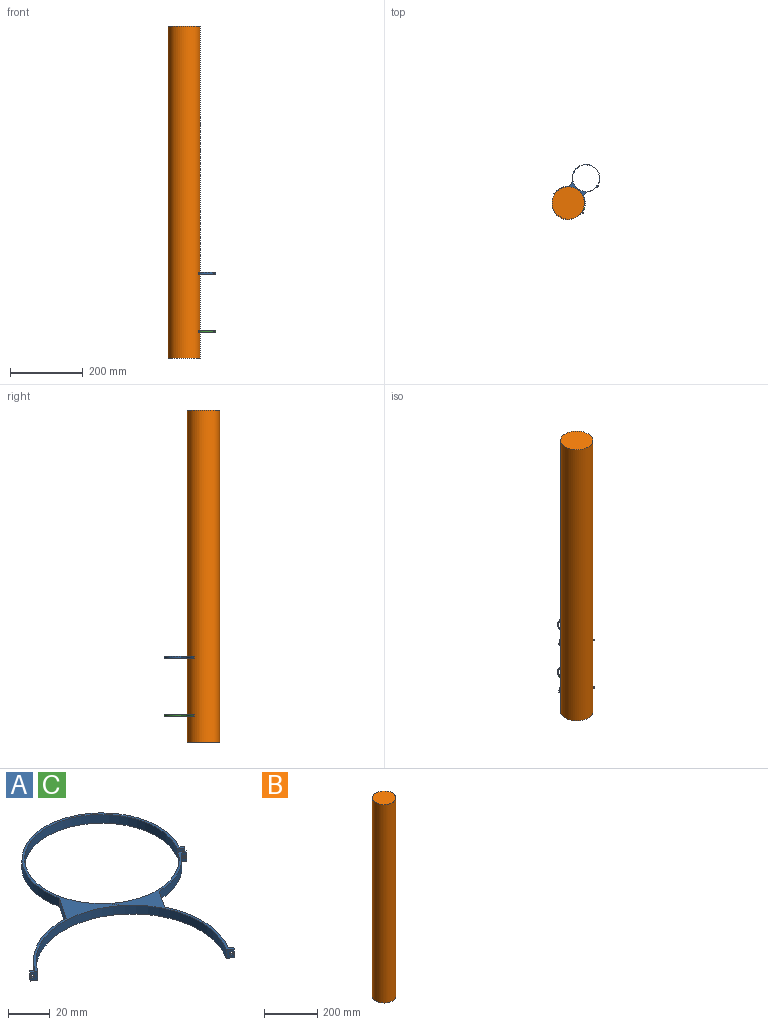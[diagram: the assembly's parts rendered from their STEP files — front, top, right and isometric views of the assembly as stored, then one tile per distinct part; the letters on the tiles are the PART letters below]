
ASSEMBLY  parts=3 mates=2
PART A: 28 faces, bbox 128.4x135x5.1 mm
  f0: cylinder r=38.1mm len=5.08mm, axis (0,0,-1), area 13.1mm2, adj f21,f22,f23
  f1: plane 5.08x3.17mm, normal (-0.55,-0.83,0), area 16.5mm2, adj f2,f20,f22,f23,f24
  f2: cylinder r=45.72mm len=83.75mm, axis (0,0,-1), area 729.7mm2, adj f1,f3,f22,f23
  f3: plane 5.08x3.17mm, normal (-0.55,-0.83,0), area 16.5mm2, adj f2,f4,f22,f23,f25
  f4: plane 5.08x1.06mm, normal (0.83,-0.55,0), area 6.5mm2, adj f3,f5,f22,f23
  f5: plane 5.08x2.13mm, normal (0.55,0.83,0), area 10.1mm2, adj f4,f6,f22,f23,f25
  f6: cylinder r=46.99mm len=45.46mm, axis (0,0,-1), area 241.4mm2, adj f5,f7,f22,f23
  f7: plane 10.89x7.26mm, normal (0.83,-0.55,0), area 66.5mm2, adj f6,f8,f22,f23
  f8: cylinder r=38.1mm len=29.75mm, axis (0,0,-1), area 174.9mm2, adj f7,f9,f22,f23
  f9: plane 5.08x2.18mm, normal (-0.55,-0.84,0), area 10.4mm2, adj f8,f10,f22,f23,f27
  f10: plane 5.08x1.06mm, normal (0.83,-0.55,0), area 6.5mm2, adj f9,f11,f22,f23
  f11: plane 5.08x3.17mm, normal (0.55,0.83,0), area 16.5mm2, adj f10,f12,f22,f23,f27
  f12: cylinder r=36.83mm len=73.66mm, axis (0,0,-1), area 1162.7mm2, adj f11,f13,f22,f23
  f13: plane 5.08x3.17mm, normal (-0.55,-0.83,0), area 16.5mm2, adj f12,f14,f22,f23,f26
  f14: plane 5.08x1.05mm, normal (0.83,-0.55,0), area 6.4mm2, adj f13,f15,f22,f23
  f15: plane 5.08x2.17mm, normal (0.55,0.83,0), area 10.4mm2, adj f14,f16,f22,f23,f26
  f16: cylinder r=38.1mm len=76.2mm, axis (0,0,-1), area 752.6mm2, adj f15,f17,f22,f23
  f17: plane 14.02x9.35mm, normal (-0.83,0.55,0), area 85.6mm2, adj f16,f18,f22,f23
  f18: cylinder r=46.99mm len=41mm, axis (0,0,-1), area 241.4mm2, adj f17,f19,f22,f23
  f19: plane 5.08x2.13mm, normal (0.55,0.83,0), area 10.1mm2, adj f18,f20,f22,f23,f24
  f20: plane 5.08x1.06mm, normal (-0.83,0.55,0), area 6.5mm2, adj f1,f19,f22,f23
  f21: cylinder r=46.99mm len=5.08mm, axis (0,0,-1), area 13.1mm2, adj f0,f22,f23
  f22: plane 135.02x128.42mm, normal (0,0,1), area 721.8mm2, adj f0,f1,f2,f3,f4,f5,f6,f7
  f23: plane 135.02x128.42mm, normal (0,0,-1), area 721.8mm2, adj f0,f1,f2,f3,f4,f5,f6,f7
  f24: cylinder r=0.95mm len=2.29mm, axis (-0.55,-0.83,0), area 7.6mm2, adj f1,f19
  f25: cylinder r=0.95mm len=2.29mm, axis (-0.55,-0.83,0), area 7.6mm2, adj f3,f5
  f26: cylinder r=0.95mm len=2.29mm, axis (-0.55,-0.84,0), area 7.5mm2, adj f13,f15
  f27: cylinder r=0.95mm len=2.3mm, axis (-0.55,-0.84,0), area 7.6mm2, adj f9,f11
PART B: 3 faces, bbox 88.9x88.9x914.4 mm
  f0: cylinder r=44.45mm len=914.4mm, axis (0,0,-1), area 255380.6mm2, adj f1,f2
  f1: plane 88.9x88.9mm, normal (0,0,1), area 6207.2mm2, adj f0
  f2: plane 88.9x88.9mm, normal (0,0,-1), area 6207.2mm2, adj f0
PART C: same geometry as A
PLACE A t=(-145.02,240.32,96.38)mm
PLACE B t=(-145.02,240.32,-134.7)mm fixed
PLACE C t=(-145.02,240.32,-64.15)mm
MATE slider A.f2 <-> B.f0  axis (0,0,1) through (-145.02,240.32,101.46)mm
MATE slider C.f18 <-> B.f0  axis (0,0,1) through (-145.02,240.32,-59.07)mm
